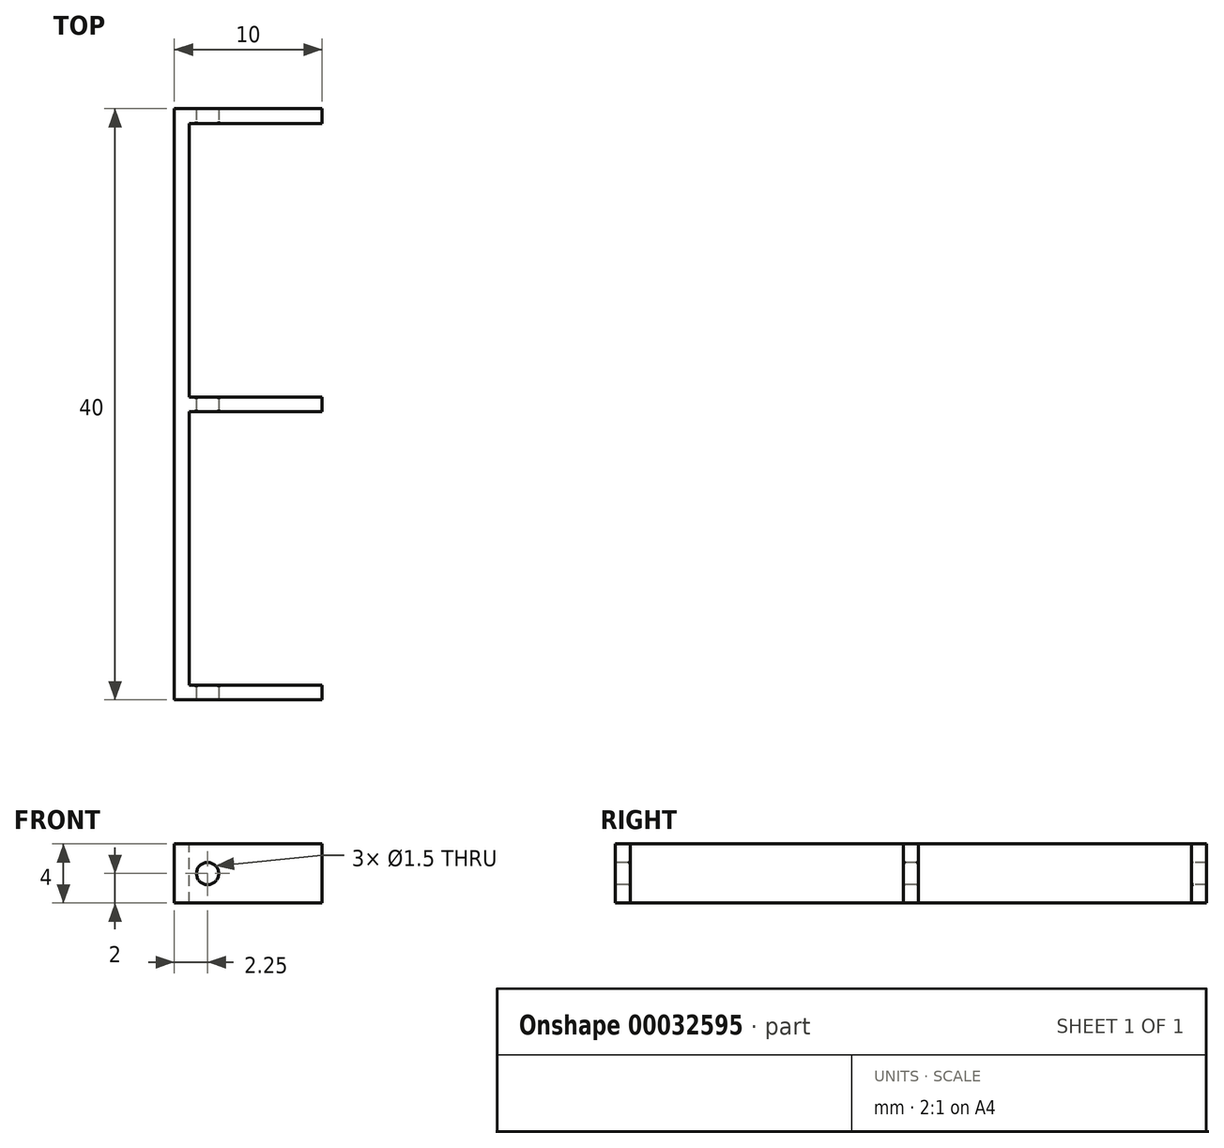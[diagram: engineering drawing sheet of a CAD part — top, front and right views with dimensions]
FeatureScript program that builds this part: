
annotation { "Feature Type Name" : "Feature", "Feature Type Description" : "" }
export const myFeature = defineFeature(function(context is Context, id is Id, definition is map)
    precondition{}
    {
        {
            assignVariable(context, id + "F0", {"name" : "Depth", "anyValue" : 8});
        }
        {
            assignVariable(context, id + "F1", {"name" : "Margin", "anyValue" : 1});
        }
        {
            var Q0;
            Q0=qCreatedBy(makeId("Top.planeOp"),FACE);
            var sketch = newSketch(context, id + "F2", { "sketchPlane" : qUnion([Q0])});
            skLineSegment(sketch, "E0.rect.bottom", {"start": v(-5, -20) * mm, "end": v(5, -20) * mm});
            skLineSegment(sketch, "E0.rect.top", {"start": v(-5, 20) * mm, "end": v(5, 20) * mm});
            skLineSegment(sketch, "E0.rect.left", {"start": v(-5, -20) * mm, "end": v(-5, 20) * mm});
            skLineSegment(sketch, "E0.rect.right", {"start": v(5, -20) * mm, "end": v(5, 20) * mm});
            skPoint(sketch, "E0.rect.middle", {"position": v(0, 0) * mm});
            skSolve(sketch);
        }
        {
            var Q0;
            Q0 = qSketchRegion(id + "F2", true);
            extrude(context, id + "F3", {"entities" : qUnion([Q0]), "depth" : (getVariable(context, 'Depth') / 2) * mm});
        }
        {
            var Q0;
            Q0=makeQuery(id+"F3.opExtrude","CAP_FACE",FACE,{"disambiguationData":[OSD([sQuery(id+"F2.wireOp",EDGE,"E0.rect.bottom"),sQuery(id+"F2.wireOp",EDGE,"E0.rect.top"),sQuery(id+"F2.wireOp",EDGE,"E0.rect.left"),sQuery(id+"F2.wireOp",EDGE,"E0.rect.right")])],"isStart":false});
            var sketch = newSketch(context, id + "F4", { "sketchPlane" : qUnion([Q0])});
            skLineSegment(sketch, "E1", {"start": v(-5, -20) * mm, "end": v(-4, -20) * mm, "construction": true});
            skLineSegment(sketch, "E2", {"start": v(-5, -20) * mm, "end": v(-5, -19) * mm, "construction": true});
            skLineSegment(sketch, "E3.bottom", {"start": v(-4, -19) * mm, "end": v(5, -19) * mm});
            skLineSegment(sketch, "E3.top", {"start": v(-4, -0.5) * mm, "end": v(5, -0.5) * mm});
            skLineSegment(sketch, "E3.left", {"start": v(-4, -19) * mm, "end": v(-4, -0.5) * mm});
            skLineSegment(sketch, "E3.right", {"start": v(5, -19) * mm, "end": v(5, -0.5) * mm});
            skLineSegment(sketch, "E4", {"start": v(-5, 0) * mm, "end": v(5, 0) * mm, "construction": true});
            skLineSegment(sketch, "E5", {"start": v(5, 19) * mm, "end": v(-4, 19) * mm});
            skLineSegment(sketch, "E6", {"start": v(-4, 19) * mm, "end": v(-4, 0.5) * mm});
            skLineSegment(sketch, "E7", {"start": v(-4, 0.5) * mm, "end": v(5, 0.5) * mm});
            skSolve(sketch);
        }
        {
            var Q0;
            {var subQ2=sQuery(id+"F4.wireOp",EDGE,"E5");Q0=makeQuery(id+"F4.imprint","IMPRINT",FACE,{"disambiguationData":[TD([[makeQuery(id+"F4.imprint","IMPRINT",EDGE,{"derivedFrom":subQ2}),1.0]])]});}
            var Q1;
            Q1=makeQuery(id+"F4.imprint","IMPRINT",FACE,{"disambiguationData":[TD([[makeQuery(id+"F4.imprint","IMPRINT",EDGE,{"derivedFrom":sQuery(id+"F4.wireOp",EDGE,"E3.bottom")}),1.0]])]});
            extrude(context, id + "F5", {"entities" : qUnion([Q0, Q1]), "operationType" : NewBodyOperationType.REMOVE, "endBound" : BoundingType.THROUGH_ALL, "oppositeDirection" : true, "depth" : 25 * mm});
        }
        {
            var Q0;
            Q0=makeQuery(id+"F3.opExtrude","SWEPT_FACE",FACE,{"disambiguationData":[OSD([sQuery(id+"F2.wireOp",EDGE,"E0.rect.bottom")])]});
            var sketch = newSketch(context, id + "F6", { "sketchPlane" : qUnion([Q0])});
            skLineSegment(sketch, "E8", {"start": v(-3.5, 4) * mm, "end": v(-3.5, 2.75) * mm, "construction": true});
            skPoint(sketch, "E9.0", {"position": v(-3.5, 0) * mm});
            skLineSegment(sketch, "E10", {"start": v(-3.5, 0) * mm, "end": v(-3.5, 1.25) * mm, "construction": true});
            skLineSegment(sketch, "E11.bottom", {"start": v(-3.5, 2.75) * mm, "end": v(-2, 2.75) * mm, "construction": true});
            skLineSegment(sketch, "E11.top", {"start": v(-3.5, 1.25) * mm, "end": v(-2, 1.25) * mm, "construction": true});
            skLineSegment(sketch, "E11.left", {"start": v(-3.5, 2.75) * mm, "end": v(-3.5, 1.25) * mm, "construction": true});
            skLineSegment(sketch, "E11.right", {"start": v(-2, 2.75) * mm, "end": v(-2, 1.25) * mm, "construction": true});
            skCircle(sketch, "E12", {"center": v(-2.75, 2) * mm, "radius": 0.75 * mm});
            skPoint(sketch, "E12.centerSnap0", {"position": v(-2, 2) * mm});
            skPoint(sketch, "E12.centerSnap1", {"position": v(-2.75, 2.75) * mm});
            skSolve(sketch);
        }
        {
            var Q0;
            Q0=makeQuery(id+"F6.imprint","IMPRINT",FACE,{"disambiguationData":[TD([[makeQuery(id+"F6.imprint","IMPRINT",EDGE,{"derivedFrom":sQuery(id+"F6.wireOp",EDGE,"E12")}),1.0]])]});
            extrude(context, id + "F7", {"entities" : qUnion([Q0]), "operationType" : NewBodyOperationType.REMOVE, "endBound" : BoundingType.THROUGH_ALL, "oppositeDirection" : true, "depth" : 25 * mm});
        }
        {
            var Q0;
            Q0=makeQuery(id+"F7.boolean.opBoolean","INTERSECT",EDGE,{"derivedFrom":[makeQuery(id+"F5.boolean.opBoolean","COPY",FACE,{"derivedFrom":makeQuery(id+"F5.opExtrude","SWEPT_FACE",FACE,{"disambiguationData":[OSD([sQuery(id+"F4.wireOp",EDGE,"E3.bottom")])]})}),makeQuery(id+"F7.opExtrude","SWEPT_FACE",FACE,{"disambiguationData":[OSD([sQuery(id+"F6.wireOp",EDGE,"E12")])]})]});
            var Q1;
            Q1=makeQuery(id+"F7.boolean.opBoolean","INTERSECT",EDGE,{"derivedFrom":[makeQuery(id+"F5.boolean.opBoolean","COPY",FACE,{"derivedFrom":makeQuery(id+"F5.opExtrude","SWEPT_FACE",FACE,{"disambiguationData":[OSD([sQuery(id+"F4.wireOp",EDGE,"E3.top")])]})}),makeQuery(id+"F7.opExtrude","SWEPT_FACE",FACE,{"disambiguationData":[OSD([sQuery(id+"F6.wireOp",EDGE,"E12")])]})]});
            var Q2;
            Q2=makeQuery(id+"F7.boolean.opBoolean","INTERSECT",EDGE,{"derivedFrom":[makeQuery(id+"F5.boolean.opBoolean","COPY",FACE,{"derivedFrom":makeQuery(id+"F5.opExtrude","SWEPT_FACE",FACE,{"disambiguationData":[OSD([sQuery(id+"F4.wireOp",EDGE,"E5")])]})}),makeQuery(id+"F7.opExtrude","SWEPT_FACE",FACE,{"disambiguationData":[OSD([sQuery(id+"F6.wireOp",EDGE,"E12")])]})]});
            var Q3;
            Q3=makeQuery(id+"F7.boolean.opBoolean","INTERSECT",EDGE,{"derivedFrom":[makeQuery(id+"F5.boolean.opBoolean","COPY",FACE,{"derivedFrom":makeQuery(id+"F5.opExtrude","SWEPT_FACE",FACE,{"disambiguationData":[OSD([sQuery(id+"F4.wireOp",EDGE,"E7")])]})}),makeQuery(id+"F7.opExtrude","SWEPT_FACE",FACE,{"disambiguationData":[OSD([sQuery(id+"F6.wireOp",EDGE,"E12")])]})]});
            fillet(context, id + "F8", {"entities" : qUnion([Q0, Q1, Q2, Q3]), "radius" : (getVariable(context, 'Margin') / 8) * mm, "tangentPropagation" : true, "allowEdgeOverflow" : false});
        }
    });
